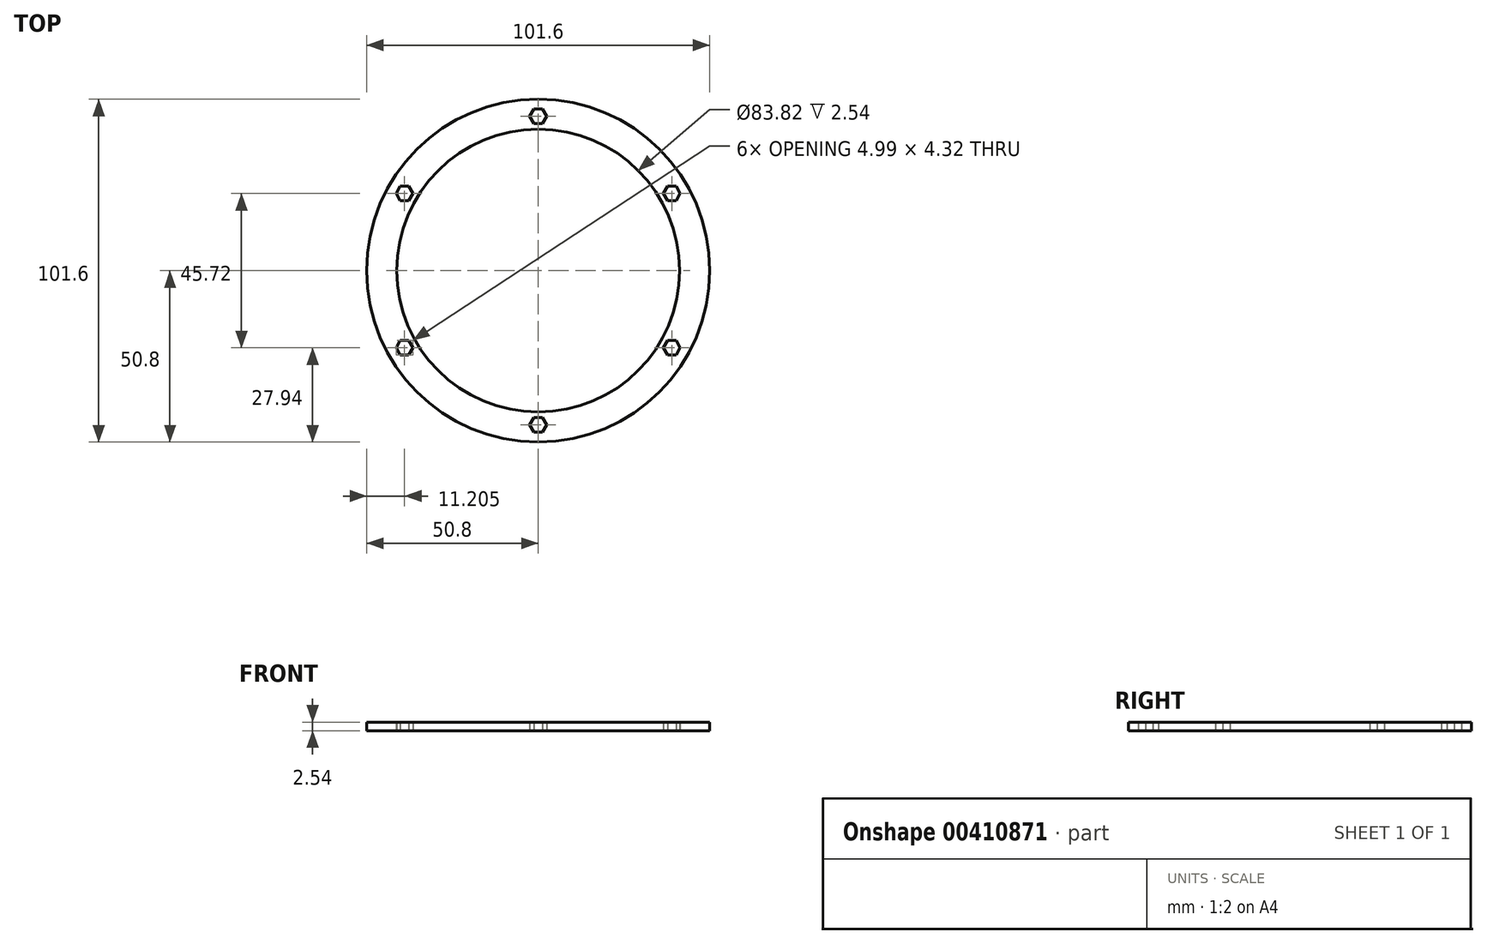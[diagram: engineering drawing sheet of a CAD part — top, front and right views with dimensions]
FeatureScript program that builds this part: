
annotation { "Feature Type Name" : "Feature", "Feature Type Description" : "" }
export const myFeature = defineFeature(function(context is Context, id is Id, definition is map)
    precondition{}
    {
        {
            var Q0;
            Q0=qCreatedBy(makeId("Top.planeOp"),FACE);
            var sketch = newSketch(context, id + "F0", { "sketchPlane" : qUnion([Q0])});
            skCircle(sketch, "E0", {"center": v(0, 0) * mm, "radius": 50.8 * mm});
            skLineSegment(sketch, "E1", {"start": v(0, 0) * mm, "end": v(0, 45.72) * mm, "construction": true});
            skCircle(sketch, "E2.cCircle", {"center": v(0, 45.72) * mm, "radius": 2.16 * mm, "construction": true});
            skLineSegment(sketch, "E2.0", {"start": v(-1.25, 47.88) * mm, "end": v(1.25, 47.88) * mm});
            skLineSegment(sketch, "E2.1", {"start": v(1.25, 47.88) * mm, "end": v(2.5, 45.72) * mm});
            skLineSegment(sketch, "E2.2", {"start": v(2.5, 45.72) * mm, "end": v(1.25, 43.56) * mm});
            skLineSegment(sketch, "E2.3", {"start": v(1.25, 43.56) * mm, "end": v(-1.25, 43.56) * mm});
            skLineSegment(sketch, "E2.4", {"start": v(-1.25, 43.56) * mm, "end": v(-2.5, 45.72) * mm});
            skLineSegment(sketch, "E2.5", {"start": v(-2.5, 45.72) * mm, "end": v(-1.25, 47.88) * mm});
            skPoint(sketch, "E2.0.midPoint", {"position": v(0, 47.88) * mm});
            skCircle(sketch, "E3", {"center": v(0, 0) * mm, "radius": 41.91 * mm});
            skLineSegment(sketch, "E4.1.0", {"start": v(-42.09, 22.86) * mm, "end": v(-40.84, 25.02) * mm});
            skLineSegment(sketch, "E4.1.1", {"start": v(-40.84, 25.02) * mm, "end": v(-38.35, 25.02) * mm});
            skLineSegment(sketch, "E4.1.2", {"start": v(-38.35, 25.02) * mm, "end": v(-37.1, 22.86) * mm});
            skLineSegment(sketch, "E4.1.3", {"start": v(-37.1, 22.86) * mm, "end": v(-38.35, 20.7) * mm});
            skLineSegment(sketch, "E4.1.4", {"start": v(-38.35, 20.7) * mm, "end": v(-40.84, 20.7) * mm});
            skLineSegment(sketch, "E4.1.5", {"start": v(-40.84, 20.7) * mm, "end": v(-42.09, 22.86) * mm});
            skLineSegment(sketch, "E4.2.0", {"start": v(-40.84, -25.02) * mm, "end": v(-42.09, -22.86) * mm});
            skLineSegment(sketch, "E4.2.1", {"start": v(-42.09, -22.86) * mm, "end": v(-40.84, -20.7) * mm});
            skLineSegment(sketch, "E4.2.2", {"start": v(-40.84, -20.7) * mm, "end": v(-38.35, -20.7) * mm});
            skLineSegment(sketch, "E4.2.3", {"start": v(-38.35, -20.7) * mm, "end": v(-37.1, -22.86) * mm});
            skLineSegment(sketch, "E4.2.4", {"start": v(-37.1, -22.86) * mm, "end": v(-38.35, -25.02) * mm});
            skLineSegment(sketch, "E4.2.5", {"start": v(-38.35, -25.02) * mm, "end": v(-40.84, -25.02) * mm});
            skLineSegment(sketch, "E4.3.0", {"start": v(1.25, -47.88) * mm, "end": v(-1.25, -47.88) * mm});
            skLineSegment(sketch, "E4.3.1", {"start": v(-1.25, -47.88) * mm, "end": v(-2.5, -45.72) * mm});
            skLineSegment(sketch, "E4.3.2", {"start": v(-2.5, -45.72) * mm, "end": v(-1.25, -43.56) * mm});
            skLineSegment(sketch, "E4.3.3", {"start": v(-1.25, -43.56) * mm, "end": v(1.25, -43.56) * mm});
            skLineSegment(sketch, "E4.3.4", {"start": v(1.25, -43.56) * mm, "end": v(2.5, -45.72) * mm});
            skLineSegment(sketch, "E4.3.5", {"start": v(2.5, -45.72) * mm, "end": v(1.25, -47.88) * mm});
            skLineSegment(sketch, "E4.4.0", {"start": v(42.09, -22.86) * mm, "end": v(40.84, -25.02) * mm});
            skLineSegment(sketch, "E4.4.1", {"start": v(40.84, -25.02) * mm, "end": v(38.35, -25.02) * mm});
            skLineSegment(sketch, "E4.4.2", {"start": v(38.35, -25.02) * mm, "end": v(37.1, -22.86) * mm});
            skLineSegment(sketch, "E4.4.3", {"start": v(37.1, -22.86) * mm, "end": v(38.35, -20.7) * mm});
            skLineSegment(sketch, "E4.4.4", {"start": v(38.35, -20.7) * mm, "end": v(40.84, -20.7) * mm});
            skLineSegment(sketch, "E4.4.5", {"start": v(40.84, -20.7) * mm, "end": v(42.09, -22.86) * mm});
            skLineSegment(sketch, "E4.5.0", {"start": v(40.84, 25.02) * mm, "end": v(42.09, 22.86) * mm});
            skLineSegment(sketch, "E4.5.1", {"start": v(42.09, 22.86) * mm, "end": v(40.84, 20.7) * mm});
            skLineSegment(sketch, "E4.5.2", {"start": v(40.84, 20.7) * mm, "end": v(38.35, 20.7) * mm});
            skLineSegment(sketch, "E4.5.3", {"start": v(38.35, 20.7) * mm, "end": v(37.1, 22.86) * mm});
            skLineSegment(sketch, "E4.5.4", {"start": v(37.1, 22.86) * mm, "end": v(38.35, 25.02) * mm});
            skLineSegment(sketch, "E4.5.5", {"start": v(38.35, 25.02) * mm, "end": v(40.84, 25.02) * mm});
            skSolve(sketch);
        }
        {
            var Q0;
            Q0=makeQuery(id+"F0.imprint","IMPRINT",FACE,{"disambiguationData":[TD([[makeQuery(id+"F0.imprint","IMPRINT",EDGE,{"derivedFrom":sQuery(id+"F0.wireOp",EDGE,"E0")}),1.0]])]});
            extrude(context, id + "F1", {"entities" : qUnion([Q0]), "depth" : 2.54 * mm});
        }
    });
